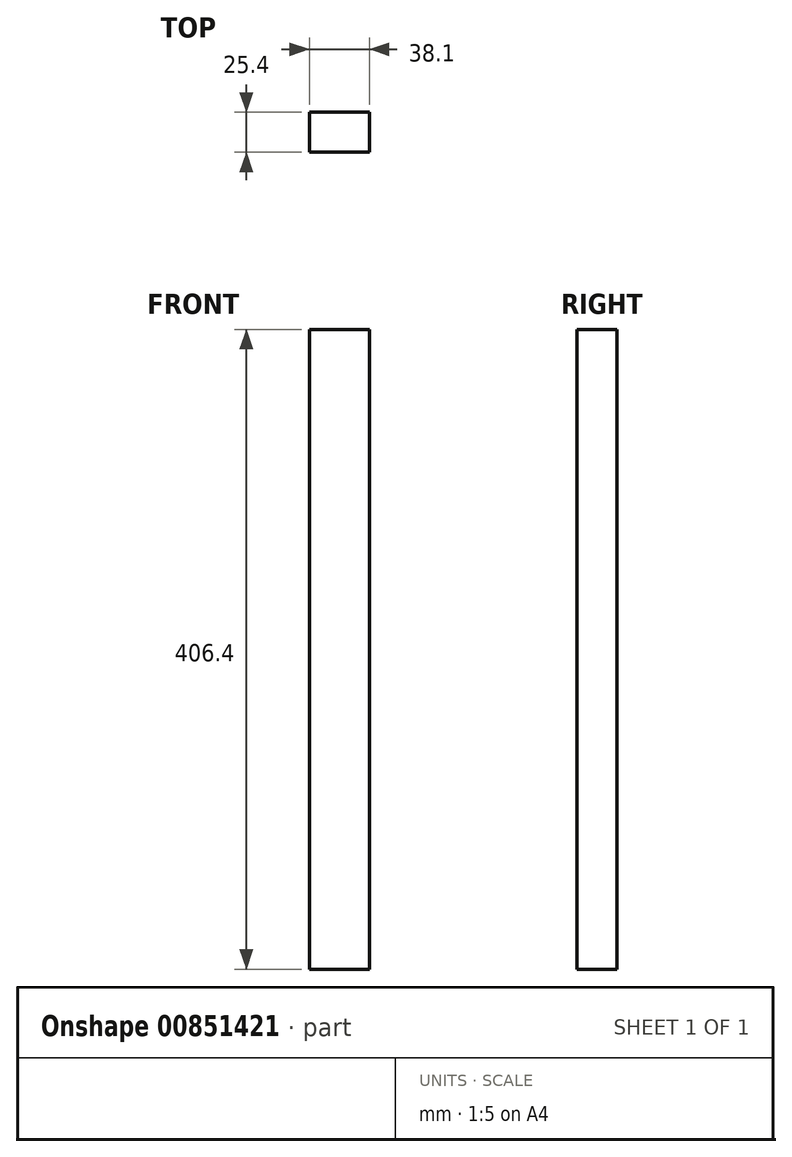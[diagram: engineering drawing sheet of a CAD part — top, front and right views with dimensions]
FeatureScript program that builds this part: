
annotation { "Feature Type Name" : "Feature", "Feature Type Description" : "" }
export const myFeature = defineFeature(function(context is Context, id is Id, definition is map)
    precondition{}
    {
        {
            var Q0;
            Q0=qCreatedBy(makeId("Front.planeOp"),FACE);
            var sketch = newSketch(context, id + "F0", { "sketchPlane" : qUnion([Q0])});
            skLineSegment(sketch, "E0.bottom", {"start": v(-27.02, 364.73) * mm, "end": v(11.08, 364.73) * mm});
            skLineSegment(sketch, "E0.top", {"start": v(-27.02, -41.67) * mm, "end": v(11.08, -41.67) * mm});
            skLineSegment(sketch, "E0.left", {"start": v(-27.02, 364.73) * mm, "end": v(-27.02, -41.67) * mm});
            skLineSegment(sketch, "E0.right", {"start": v(11.08, 364.73) * mm, "end": v(11.08, -41.67) * mm});
            skSolve(sketch);
        }
        {
            var Q0;
            Q0 = qSketchRegion(id + "F0", true);
            extrude(context, id + "F1", {"entities" : qUnion([Q0]), "depth" : 25.4 * mm, "offsetDistance" : 25.4 * mm});
        }
    });
